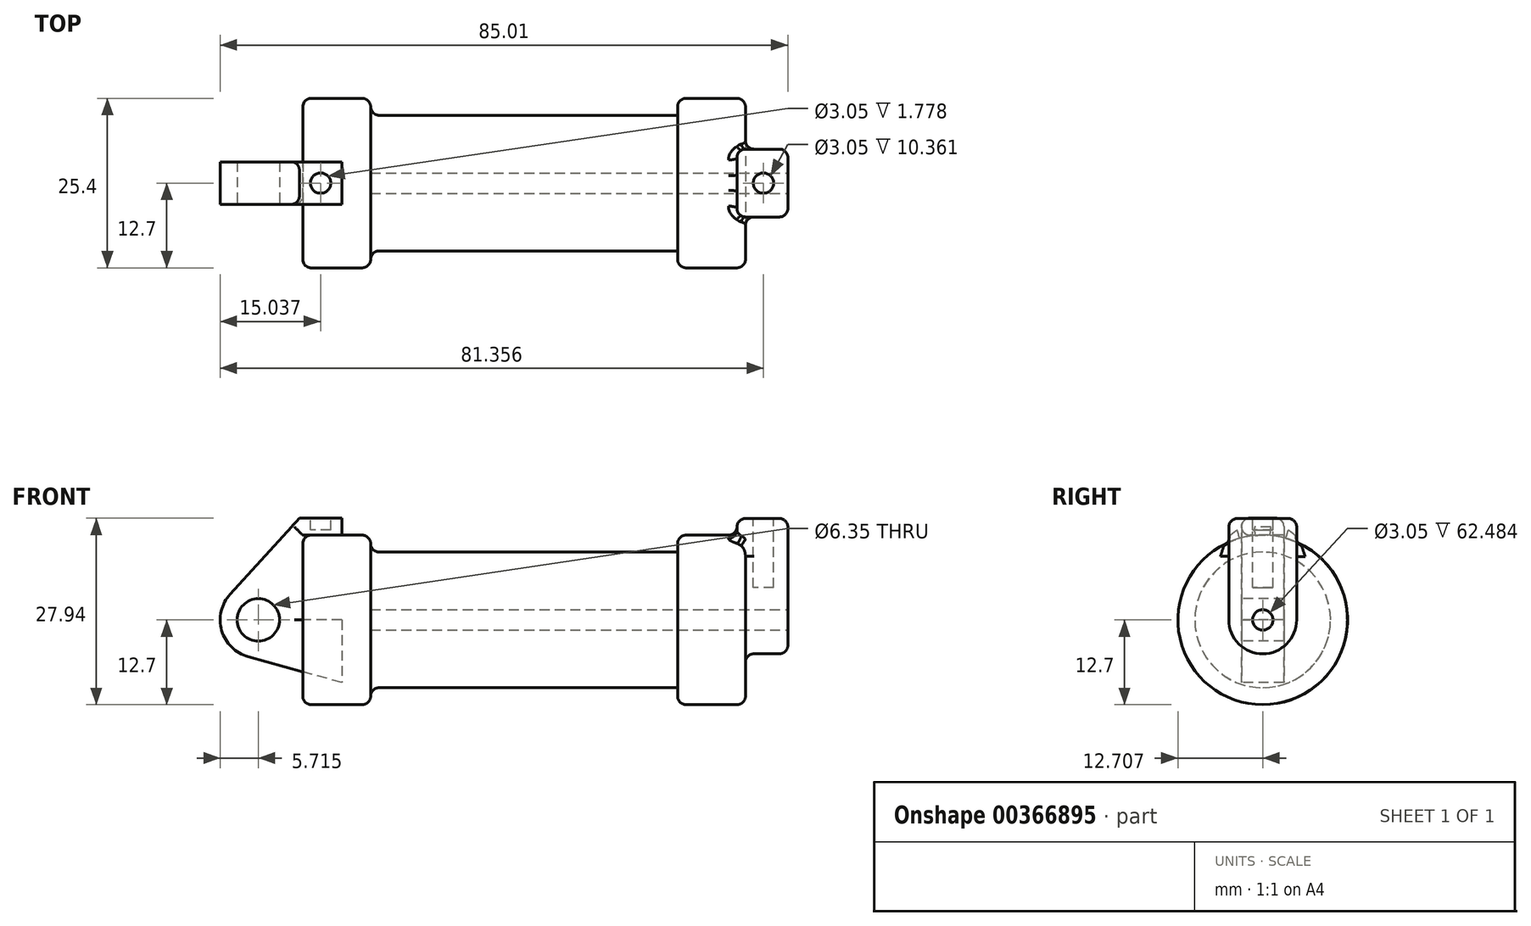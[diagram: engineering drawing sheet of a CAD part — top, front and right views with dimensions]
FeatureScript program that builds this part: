
annotation { "Feature Type Name" : "Feature", "Feature Type Description" : "" }
export const myFeature = defineFeature(function(context is Context, id is Id, definition is map)
    precondition{}
    {
        {
            var Q0;
            Q0=qCreatedBy(makeId("Front.planeOp"),FACE);
            var sketch = newSketch(context, id + "F0", { "sketchPlane" : qUnion([Q0])});
            skLineSegment(sketch, "E0", {"start": v(0, 0) * mm, "end": v(0, 12.7) * mm});
            skLineSegment(sketch, "E1", {"start": v(0, 12.7) * mm, "end": v(10.16, 12.7) * mm});
            skLineSegment(sketch, "E2", {"start": v(10.16, 12.7) * mm, "end": v(10.16, 10.16) * mm});
            skLineSegment(sketch, "E3", {"start": v(10.16, 10.16) * mm, "end": v(56.13, 10.16) * mm});
            skLineSegment(sketch, "E4", {"start": v(56.13, 10.16) * mm, "end": v(56.13, 12.7) * mm});
            skLineSegment(sketch, "E5", {"start": v(56.13, 12.7) * mm, "end": v(66.3, 12.7) * mm});
            skLineSegment(sketch, "E6", {"start": v(66.3, 12.7) * mm, "end": v(66.3, 0) * mm});
            skLineSegment(sketch, "E7", {"start": v(66.3, 0) * mm, "end": v(0, 0) * mm});
            skLineSegment(sketch, "E8", {"start": v(5.84, 15.24) * mm, "end": v(-0.5, 15.24) * mm});
            skLineSegment(sketch, "E9", {"start": v(-0.5, 15.24) * mm, "end": v(-10.88, 3.85) * mm});
            skLineSegment(sketch, "E10", {"start": v(0, 0) * mm, "end": v(-6.65, 0) * mm});
            skCircle(sketch, "E11", {"center": v(-6.65, 0) * mm, "radius": 5.72 * mm});
            skCircle(sketch, "E12", {"center": v(-6.65, 0) * mm, "radius": 3.18 * mm});
            skLineSegment(sketch, "E13", {"start": v(5.84, 15.24) * mm, "end": v(5.84, -9.4) * mm});
            skLineSegment(sketch, "E14", {"start": v(5.84, -9.4) * mm, "end": v(-8.18, -5.5) * mm});
            skSolve(sketch);
        }
        {
            var Q0;
            {var subQ0=sQuery(id+"F0.wireOp",EDGE,"E2");Q0=makeQuery(id+"F0.imprint","IMPRINT",FACE,{"disambiguationData":[TD([[makeQuery(id+"F0.imprint","IMPRINT",EDGE,{"derivedFrom":subQ0}),-1.0]])]});}
            var Q1;
            {var subQ0=sQuery(id+"F0.wireOp",EDGE,"E0");Q1=makeQuery(id+"F0.imprint","IMPRINT",FACE,{"disambiguationData":[TD([[makeQuery(id+"F0.imprint","IMPRINT",EDGE,{"derivedFrom":subQ0}),-1.0]])]});}
            var Q2;
            Q2=sQuery(id+"F0.wireOp",EDGE,"E7");
            revolve(context, id + "F1", {"entities" : qUnion([Q0, Q1]), "axis" : qUnion([Q2]), "revolveType" : RevolveType.FULL});
        }
        {
            var Q0;
            {var subQ1=sQuery(id+"F0.wireOp",EDGE,"E0");Q0=makeQuery(id+"F0.imprint","IMPRINT",FACE,{"disambiguationData":[TD([[makeQuery(id+"F0.imprint","IMPRINT",EDGE,{"derivedFrom":subQ1}),1.0]])]});}
            var Q1;
            {var subQ5=sQuery(id+"F0.wireOp",EDGE,"E12");Q1=makeQuery(id+"F0.imprint","IMPRINT",FACE,{"disambiguationData":[TD([[makeQuery(id+"F0.imprint","IMPRINT",EDGE,{"derivedFrom":subQ5}),-1.0]])]});}
            var Q2;
            {var subQ0=sQuery(id+"F0.wireOp",EDGE,"E14");Q2=makeQuery(id+"F0.imprint","IMPRINT",FACE,{"disambiguationData":[TD([[makeQuery(id+"F0.imprint","IMPRINT",EDGE,{"derivedFrom":subQ0}),-1.0]])]});}
            extrude(context, id + "F2", {"entities" : qUnion([Q0, Q1, Q2]), "endBound" : BoundingType.SYMMETRIC, "oppositeDirection" : true, "depth" : 6.35 * mm});
        }
        {
            var Q0;
            Q0=makeQuery(id+"F1.opRevolve","SWEPT_FACE",FACE,{"disambiguationData":[OSD([sQuery(id+"F0.wireOp",EDGE,"E6")])]});
            var sketch = newSketch(context, id + "F3", { "sketchPlane" : qUnion([Q0])});
            skCircle(sketch, "E15", {"center": v(0, 0) * mm, "radius": 1.52 * mm});
            skCircle(sketch, "E16", {"center": v(0, 0) * mm, "radius": 5.08 * mm});
            skLineSegment(sketch, "E17", {"start": v(-5.07, 0) * mm, "end": v(-5.07, 15.19) * mm});
            skLineSegment(sketch, "E18", {"start": v(-5.07, 15.19) * mm, "end": v(5.09, 15.19) * mm});
            skLineSegment(sketch, "E19", {"start": v(5.09, 15.19) * mm, "end": v(5.09, 0) * mm});
            skSolve(sketch);
        }
        {
            var Q0;
            Q0=makeQuery(id+"F3.imprint","IMPRINT",FACE,{"disambiguationData":[TD([[makeQuery(id+"F3.imprint","IMPRINT",EDGE,{"derivedFrom":sQuery(id+"F3.wireOp",EDGE,"E15")}),1.0]])]});
            var Q1;
            Q1=makeQuery(id+"F1.opRevolve","SWEPT_FACE",FACE,{"disambiguationData":[OSD([sQuery(id+"F0.wireOp",EDGE,"E2")])]});
            extrude(context, id + "F4", {"entities" : qUnion([Q0]), "operationType" : NewBodyOperationType.REMOVE, "endBound" : BoundingType.UP_TO_SURFACE, "oppositeDirection" : true, "endBoundEntityFace" : qUnion([Q1]), "depth" : 25.4 * mm});
        }
        {
            var Q0;
            {var subQ0=sQuery(id+"F3.wireOp",EDGE,"E17");var subQ1=sQuery(id+"F3.wireOp",EDGE,"E16");var subQ2=makeQuery(id+"F3.imprint","INTERSECT",VERTEX,{"derivedFrom":[subQ1,subQ0]});Q0=makeQuery(id+"F3.imprint","IMPRINT",FACE,{"disambiguationData":[TD([[makeQuery(id+"F3.imprint","IMPRINT",EDGE,{"disambiguationData":[TD([[subQ2,1.0]])],"derivedFrom":subQ1}),-1.0]])]});}
            var Q1;
            {var subQ0=sQuery(id+"F3.wireOp",EDGE,"E18");Q1=makeQuery(id+"F3.imprint","IMPRINT",FACE,{"disambiguationData":[TD([[makeQuery(id+"F3.imprint","IMPRINT",EDGE,{"derivedFrom":subQ0}),-1.0]])]});}
            var Q2;
            Q2=makeQuery(id+"F3.imprint","IMPRINT",FACE,{"disambiguationData":[TD([[makeQuery(id+"F3.imprint","IMPRINT",EDGE,{"derivedFrom":sQuery(id+"F3.wireOp",EDGE,"E15")}),-1.0]])]});
            extrude(context, id + "F5", {"entities" : qUnion([Q0, Q1, Q2]), "operationType" : NewBodyOperationType.ADD, "oppositeDirection" : true, "depth" : 1.27 * mm});
        }
        {
            var Q0;
            {var subQ0=sQuery(id+"F3.wireOp",EDGE,"E17");var subQ1=sQuery(id+"F3.wireOp",EDGE,"E16");var subQ2=makeQuery(id+"F3.imprint","INTERSECT",VERTEX,{"derivedFrom":[subQ1,subQ0]});Q0=makeQuery(id+"F3.imprint","IMPRINT",FACE,{"disambiguationData":[TD([[makeQuery(id+"F3.imprint","IMPRINT",EDGE,{"disambiguationData":[TD([[subQ2,1.0]])],"derivedFrom":subQ1}),-1.0]])]});}
            var Q1;
            {var subQ0=sQuery(id+"F3.wireOp",EDGE,"E18");Q1=makeQuery(id+"F3.imprint","IMPRINT",FACE,{"disambiguationData":[TD([[makeQuery(id+"F3.imprint","IMPRINT",EDGE,{"derivedFrom":subQ0}),-1.0]])]});}
            var Q2;
            Q2=makeQuery(id+"F3.imprint","IMPRINT",FACE,{"disambiguationData":[TD([[makeQuery(id+"F3.imprint","IMPRINT",EDGE,{"derivedFrom":sQuery(id+"F3.wireOp",EDGE,"E15")}),-1.0]])]});
            extrude(context, id + "F6", {"entities" : qUnion([Q0, Q1, Q2]), "operationType" : NewBodyOperationType.ADD, "depth" : 6.35 * mm});
        }
        {
            var Q0;
            Q0=makeQuery(id+"F2.opExtrude","SWEPT_FACE",FACE,{"disambiguationData":[OSD([sQuery(id+"F0.wireOp",EDGE,"E8")])]});
            var sketch = newSketch(context, id + "F7", { "sketchPlane" : qUnion([Q0])});
            skLineSegment(sketch, "E20", {"start": v(5.84, 0) * mm, "end": v(-0.5, 0) * mm, "construction": true});
            skLineSegment(sketch, "E21", {"start": v(65.34, 0.16) * mm, "end": v(72.63, 0.16) * mm, "construction": true});
            skLineSegment(sketch, "E22", {"start": v(65.34, 0.16) * mm, "end": v(72.63, 0.16) * mm});
            skCircle(sketch, "E23", {"center": v(2.67, 0) * mm, "radius": 1.52 * mm});
            skCircle(sketch, "E24", {"center": v(68.99, 0) * mm, "radius": 1.52 * mm});
            skPoint(sketch, "E24.centerSnap0", {"position": v(68.99, 0.16) * mm});
            skSolve(sketch);
        }
        {
            var Q0;
            Q0=makeQuery(id+"F7.imprint","IMPRINT",FACE,{"disambiguationData":[TD([[makeQuery(id+"F7.imprint","IMPRINT",EDGE,{"derivedFrom":sQuery(id+"F7.wireOp",EDGE,"E23")}),1.0]])]});
            extrude(context, id + "F8", {"entities" : qUnion([Q0]), "operationType" : NewBodyOperationType.REMOVE, "oppositeDirection" : true, "depth" : 1.78 * mm});
        }
        {
            var Q0;
            {var subQ0=sQuery(id+"F7.wireOp",EDGE,"E24");var subQ1=sQuery(id+"F7.wireOp",EDGE,"E22");var subQ2=makeQuery(id+"F7.imprint","INTERSECT",VERTEX,{"disambiguationData":[OD(0.0)],"derivedFrom":[subQ1,subQ0]});Q0=makeQuery(id+"F7.imprint","IMPRINT",FACE,{"disambiguationData":[TD([[makeQuery(id+"F7.imprint","IMPRINT",EDGE,{"disambiguationData":[TD([[subQ2,-1.0]])],"derivedFrom":subQ1}),-1.0]])]});}
            var Q1;
            {var subQ0=sQuery(id+"F7.wireOp",EDGE,"E24");var subQ1=sQuery(id+"F7.wireOp",EDGE,"E22");var subQ2=makeQuery(id+"F7.imprint","INTERSECT",VERTEX,{"disambiguationData":[OD(0.0)],"derivedFrom":[subQ1,subQ0]});Q1=makeQuery(id+"F7.imprint","IMPRINT",FACE,{"disambiguationData":[TD([[makeQuery(id+"F7.imprint","IMPRINT",EDGE,{"disambiguationData":[TD([[subQ2,-1.0]])],"derivedFrom":subQ1}),1.0]])]});}
            extrude(context, id + "F9", {"entities" : qUnion([Q0, Q1]), "operationType" : NewBodyOperationType.REMOVE, "oppositeDirection" : true, "depth" : 10.4 * mm});
        }
        {
            var Q0;
            Q0=makeQuery(id+"F1.opRevolve","SWEPT_EDGE",EDGE,{"disambiguationData":[OSD([sQuery(id+"F0.wireOp",EDGE,"E1"),sQuery(id+"F0.wireOp",EDGE,"E2")])]});
            fillet(context, id + "F10", {"entities" : qUnion([Q0]), "radius" : 1.27 * mm, "tangentPropagation" : true, "allowEdgeOverflow" : false});
        }
        {
            var Q0;
            Q0=makeQuery(id+"F1.opRevolve","SWEPT_EDGE",EDGE,{"disambiguationData":[OSD([sQuery(id+"F0.wireOp",EDGE,"E2"),sQuery(id+"F0.wireOp",EDGE,"E3")])]});
            fillet(context, id + "F11", {"entities" : qUnion([Q0]), "radius" : 1.27 * mm, "tangentPropagation" : true, "allowEdgeOverflow" : false});
        }
        {
            var Q0;
            Q0=makeQuery(id+"F1.opRevolve","SWEPT_EDGE",EDGE,{"disambiguationData":[OSD([sQuery(id+"F0.wireOp",EDGE,"E0"),sQuery(id+"F0.wireOp",EDGE,"E1")])]});
            fillet(context, id + "F12", {"entities" : qUnion([Q0]), "radius" : 1.27 * mm, "tangentPropagation" : true, "allowEdgeOverflow" : false});
        }
        {
            var Q0;
            Q0=makeQuery(id+"F1.opRevolve","SWEPT_EDGE",EDGE,{"disambiguationData":[OSD([sQuery(id+"F0.wireOp",EDGE,"E4"),sQuery(id+"F0.wireOp",EDGE,"E5")])]});
            fillet(context, id + "F13", {"entities" : qUnion([Q0]), "radius" : 1.27 * mm, "tangentPropagation" : true, "allowEdgeOverflow" : false});
        }
        {
            var Q0;
            Q0=makeQuery(id+"F1.opRevolve","SWEPT_EDGE",EDGE,{"disambiguationData":[OSD([sQuery(id+"F0.wireOp",EDGE,"E5"),sQuery(id+"F0.wireOp",EDGE,"E6")])]});
            fillet(context, id + "F14", {"entities" : qUnion([Q0]), "radius" : 1.27 * mm, "tangentPropagation" : true, "allowEdgeOverflow" : false});
        }
        {
            var Q0;
            Q0=makeQuery(id+"F6.opExtrude","CAP_EDGE",EDGE,{"disambiguationData":[OSD([sQuery(id+"F3.wireOp",EDGE,"E17")])],"isStart":false});
            var Q1;
            Q1=makeQuery(id+"F6.opExtrude","CAP_EDGE",EDGE,{"disambiguationData":[OSD([sQuery(id+"F3.wireOp",EDGE,"E16")])],"isStart":false});
            var Q2;
            Q2=makeQuery(id+"F6.opExtrude","CAP_EDGE",EDGE,{"disambiguationData":[OSD([sQuery(id+"F3.wireOp",EDGE,"E19")])],"isStart":false});
            var Q3;
            Q3=makeQuery(id+"F6.opExtrude","CAP_EDGE",EDGE,{"disambiguationData":[OSD([sQuery(id+"F3.wireOp",EDGE,"E18")])],"isStart":false});
            fillet(context, id + "F15", {"entities" : qUnion([Q0, Q1, Q2, Q3]), "radius" : 1.27 * mm, "tangentPropagation" : true, "allowEdgeOverflow" : false});
        }
        {
            var Q0;
            {var subQ0=sQuery(id+"F3.wireOp",EDGE,"E19");var subQ1=sQuery(id+"F3.wireOp",EDGE,"E18");Q0=makeQuery(id+"F6.boolean.opBoolean","MERGE",EDGE,{"derivedFrom":[makeQuery(id+"F5.opExtrude","SWEPT_EDGE",EDGE,{"disambiguationData":[OSD([subQ1,subQ0])]}),makeQuery(id+"F6.opExtrude","SWEPT_EDGE",EDGE,{"disambiguationData":[OSD([subQ1,subQ0])]})]});}
            var Q1;
            {var subQ0=sQuery(id+"F3.wireOp",EDGE,"E18");var subQ1=sQuery(id+"F3.wireOp",EDGE,"E17");Q1=makeQuery(id+"F6.boolean.opBoolean","MERGE",EDGE,{"derivedFrom":[makeQuery(id+"F5.opExtrude","SWEPT_EDGE",EDGE,{"disambiguationData":[OSD([subQ1,subQ0])]}),makeQuery(id+"F6.opExtrude","SWEPT_EDGE",EDGE,{"disambiguationData":[OSD([subQ1,subQ0])]})]});}
            var Q2;
            Q2=makeQuery(id+"F5.opExtrude","CAP_EDGE",EDGE,{"disambiguationData":[OSD([sQuery(id+"F3.wireOp",EDGE,"E18")])],"isStart":false});
            fillet(context, id + "F16", {"entities" : qUnion([Q0, Q1, Q2]), "radius" : 1.27 * mm, "tangentPropagation" : true, "allowEdgeOverflow" : false});
        }
        {
            var Q0;
            Q0=makeQuery(id+"F5.opExtrude","CAP_EDGE",EDGE,{"disambiguationData":[OSD([sQuery(id+"F3.wireOp",EDGE,"E17")])],"isStart":false});
            fillet(context, id + "F17", {"entities" : qUnion([Q0]), "radius" : 1.27 * mm, "tangentPropagation" : true, "allowEdgeOverflow" : false});
        }
        {
            var Q0;
            Q0=makeQuery(id+"F5.opExtrude","CAP_EDGE",EDGE,{"disambiguationData":[OSD([sQuery(id+"F3.wireOp",EDGE,"E19")])],"isStart":false});
            fillet(context, id + "F18", {"entities" : qUnion([Q0]), "radius" : 1.27 * mm, "tangentPropagation" : true, "allowEdgeOverflow" : false});
        }
        {
            var Q0;
            Q0=makeQuery(id+"F5.boolean.opBoolean","INTERSECT",EDGE,{"derivedFrom":[makeQuery(id+"F1.opRevolve","SWEPT_FACE",FACE,{"disambiguationData":[OSD([sQuery(id+"F0.wireOp",EDGE,"E5")])]}),makeQuery(id+"F5.opExtrude","CAP_FACE",FACE,{"disambiguationData":[OSD([sQuery(id+"F3.wireOp",EDGE,"E15"),sQuery(id+"F3.wireOp",EDGE,"E16"),sQuery(id+"F3.wireOp",EDGE,"E17"),sQuery(id+"F3.wireOp",EDGE,"E18"),sQuery(id+"F3.wireOp",EDGE,"E19")])],"isStart":false})]});
            fillet(context, id + "F19", {"entities" : qUnion([Q0]), "radius" : 1.27 * mm, "tangentPropagation" : true, "allowEdgeOverflow" : false});
        }
        {
            var Q0;
            Q0=makeQuery(id+"F2.opExtrude","CAP_EDGE",EDGE,{"disambiguationData":[OSD([sQuery(id+"F0.wireOp",EDGE,"E8")])],"isStart":false});
            fillet(context, id + "F20", {"entities" : qUnion([Q0]), "radius" : 1.27 * mm, "tangentPropagation" : true, "allowEdgeOverflow" : false});
        }
        {
            var Q0;
            Q0=makeQuery(id+"F2.opExtrude","CAP_EDGE",EDGE,{"disambiguationData":[OSD([sQuery(id+"F0.wireOp",EDGE,"E0")])],"isStart":true});
            var Q1;
            Q1=makeQuery(id+"F2.opExtrude","CAP_EDGE",EDGE,{"disambiguationData":[OSD([sQuery(id+"F0.wireOp",EDGE,"E1")])],"isStart":true});
            var Q2;
            Q2=makeQuery(id+"F2.opExtrude","CAP_EDGE",EDGE,{"disambiguationData":[OSD([sQuery(id+"F0.wireOp",EDGE,"E8")])],"isStart":true});
            fillet(context, id + "F21", {"entities" : qUnion([Q0, Q1, Q2]), "radius" : 1.27 * mm, "tangentPropagation" : true, "allowEdgeOverflow" : false});
        }
    });
